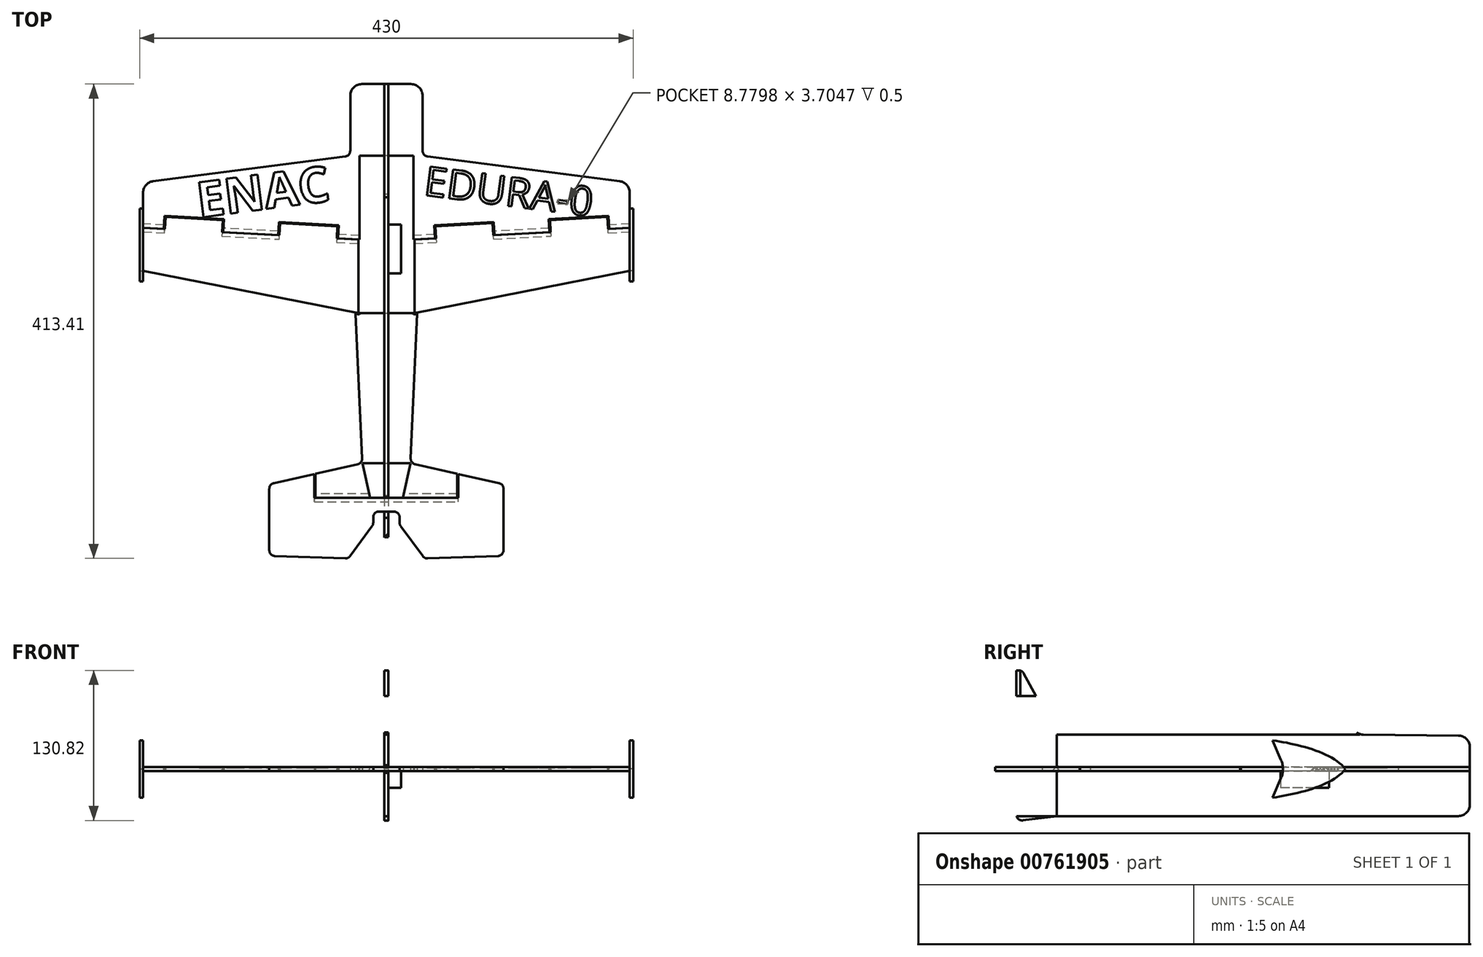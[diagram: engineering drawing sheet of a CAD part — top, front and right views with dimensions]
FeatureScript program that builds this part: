
annotation { "Feature Type Name" : "Feature", "Feature Type Description" : "" }
export const myFeature = defineFeature(function(context is Context, id is Id, definition is map)
    precondition{}
    {
        {
            assignVariable(context, id + "F0", {"name" : "strength", "anyValue" : 3.5 * mm});
        }
        {
            var Q0;
            Q0=qCreatedBy(makeId("Top.planeOp"),FACE);
            var sketch = newSketch(context, id + "F1", { "sketchPlane" : qUnion([Q0])});
            skLineSegment(sketch, "E0.bottom", {"start": v(31.5, 68.5) * mm, "end": v(-31.5, 68.5) * mm});
            skPoint(sketch, "E0.middle", {"position": v(0, 0) * mm});
            skLineSegment(sketch, "E1", {"start": v(-35.86, 67.94) * mm, "end": v(-203.28, 46.3) * mm});
            skLineSegment(sketch, "E2", {"start": v(-212, 36.4) * mm, "end": v(-212, -31.82) * mm});
            skLineSegment(sketch, "E3.MirrorCS", {"start": v(35.86, 67.94) * mm, "end": v(203.28, 46.3) * mm});
            skLineSegment(sketch, "E4.MirrorCS", {"start": v(212, 36.4) * mm, "end": v(212, -31.82) * mm});
            skLineSegment(sketch, "E5.bottom", {"start": v(-31.5, 68.5) * mm, "end": v(31.5, 68.5) * mm});
            skLineSegment(sketch, "E5.top", {"start": v(-21.5, 131) * mm, "end": v(21.5, 131) * mm});
            skLineSegment(sketch, "E5.left", {"start": v(-31.5, 72.9) * mm, "end": v(-31.5, 121) * mm});
            skLineSegment(sketch, "E5.right", {"start": v(31.5, 72.9) * mm, "end": v(31.5, 121) * mm});
            skLineSegment(sketch, "E6.top", {"start": v(-21, -199.5) * mm, "end": v(21, -199.5) * mm});
            skLineSegment(sketch, "E7", {"start": v(26.75, -69.08) * mm, "end": v(21.18, -195.31) * mm});
            skLineSegment(sketch, "E8", {"start": v(-26.75, -69.08) * mm, "end": v(-21.18, -195.31) * mm});
            skPoint(sketch, "E9.visualSharp", {"position": v(31.5, 131) * mm});
            skArc(sketch, "E9.filletArc", {"start": v(31.5, 121) * mm, "mid": v(28.57, 128.07) * mm, "end": v(21.5, 131) * mm});
            skPoint(sketch, "E10.visualSharp", {"position": v(-31.5, 131) * mm});
            skArc(sketch, "E10.filletArc", {"start": v(-21.5, 131) * mm, "mid": v(-28.57, 128.07) * mm, "end": v(-31.5, 121) * mm});
            skPoint(sketch, "E11.visualSharp", {"position": v(-212, 45.18) * mm});
            skArc(sketch, "E11.filletArc", {"start": v(-203.28, 46.3) * mm, "mid": v(-209.51, 43) * mm, "end": v(-212, 36.4) * mm});
            skPoint(sketch, "E12.visualSharp", {"position": v(212, 45.18) * mm});
            skArc(sketch, "E12.filletArc", {"start": v(212, 36.4) * mm, "mid": v(209.51, 43) * mm, "end": v(203.28, 46.3) * mm});
            skLineSegment(sketch, "E13.bottom", {"start": v(21, -199.5) * mm, "end": v(-21, -199.5) * mm});
            skLineSegment(sketch, "E14", {"start": v(-102, -221.62) * mm, "end": v(-102, -275.28) * mm});
            skLineSegment(sketch, "E15", {"start": v(-97.17, -280.28) * mm, "end": v(-35.88, -282.4) * mm});
            skLineSegment(sketch, "E16.MirrorCS", {"start": v(102, -221.62) * mm, "end": v(102, -275.28) * mm});
            skLineSegment(sketch, "E17.MirrorCS", {"start": v(97.17, -280.28) * mm, "end": v(35.88, -282.4) * mm});
            skPoint(sketch, "E18", {"position": v(0, 68.5) * mm});
            skPoint(sketch, "E19", {"position": v(0, -68.5) * mm});
            skPoint(sketch, "E20.visualSharp", {"position": v(102, -217.61) * mm});
            skArc(sketch, "E20.filletArc", {"start": v(102, -221.62) * mm, "mid": v(100.9, -218.5) * mm, "end": v(98.1, -216.74) * mm});
            skPoint(sketch, "E21.visualSharp", {"position": v(-102, -217.61) * mm});
            skArc(sketch, "E21.filletArc", {"start": v(-98.1, -216.74) * mm, "mid": v(-100.9, -218.5) * mm, "end": v(-102, -221.62) * mm});
            skLineSegment(sketch, "E22", {"start": v(6.5, -241.5) * mm, "end": v(-6.5, -241.5) * mm});
            skLineSegment(sketch, "E23", {"start": v(-21, -199.5) * mm, "end": v(-11.5, -241.5) * mm});
            skLineSegment(sketch, "E24", {"start": v(-11.5, -246.5) * mm, "end": v(-11.5, -251.36) * mm});
            skLineSegment(sketch, "E25", {"start": v(-12.48, -254.32) * mm, "end": v(-31.69, -280.38) * mm});
            skLineSegment(sketch, "E26.MirrorCS", {"start": v(21, -199.5) * mm, "end": v(11.5, -241.5) * mm});
            skLineSegment(sketch, "E27.MirrorCS", {"start": v(11.5, -246.5) * mm, "end": v(11.5, -251.36) * mm});
            skLineSegment(sketch, "E28.MirrorCS", {"start": v(12.48, -254.32) * mm, "end": v(31.69, -280.38) * mm});
            skPoint(sketch, "E29.visualSharp", {"position": v(-102, -280.11) * mm});
            skArc(sketch, "E29.filletArc", {"start": v(-102, -275.28) * mm, "mid": v(-100.6, -278.76) * mm, "end": v(-97.17, -280.28) * mm});
            skPoint(sketch, "E30.visualSharp", {"position": v(102, -280.11) * mm});
            skArc(sketch, "E30.filletArc", {"start": v(97.17, -280.28) * mm, "mid": v(100.6, -278.76) * mm, "end": v(102, -275.28) * mm});
            skPoint(sketch, "E31.visualSharp", {"position": v(33.25, -282.5) * mm});
            skArc(sketch, "E31.filletArc", {"start": v(31.69, -280.38) * mm, "mid": v(33.53, -281.91) * mm, "end": v(35.88, -282.4) * mm});
            skPoint(sketch, "E32.visualSharp", {"position": v(-33.25, -282.5) * mm});
            skArc(sketch, "E32.filletArc", {"start": v(-35.88, -282.4) * mm, "mid": v(-33.53, -281.91) * mm, "end": v(-31.69, -280.38) * mm});
            skPoint(sketch, "E33.visualSharp", {"position": v(11.5, -241.5) * mm});
            skArc(sketch, "E33.filletArc", {"start": v(11.5, -246.5) * mm, "mid": v(10.04, -242.96) * mm, "end": v(6.5, -241.5) * mm});
            skPoint(sketch, "E34.visualSharp", {"position": v(-11.5, -241.5) * mm});
            skArc(sketch, "E34.filletArc", {"start": v(-6.5, -241.5) * mm, "mid": v(-10.04, -242.96) * mm, "end": v(-11.5, -246.5) * mm});
            skPoint(sketch, "E35.visualSharp", {"position": v(-11.5, -253) * mm});
            skArc(sketch, "E35.filletArc", {"start": v(-12.48, -254.32) * mm, "mid": v(-11.75, -252.92) * mm, "end": v(-11.5, -251.36) * mm});
            skPoint(sketch, "E36.visualSharp", {"position": v(11.5, -253) * mm});
            skArc(sketch, "E36.filletArc", {"start": v(11.5, -251.36) * mm, "mid": v(11.75, -252.92) * mm, "end": v(12.48, -254.32) * mm});
            skPoint(sketch, "E37.visualSharp", {"position": v(31.5, 68.5) * mm});
            skArc(sketch, "E37.filletArc", {"start": v(31.5, 72.9) * mm, "mid": v(32.74, 69.6) * mm, "end": v(35.86, 67.94) * mm});
            skPoint(sketch, "E38.visualSharp", {"position": v(-31.5, 68.5) * mm});
            skArc(sketch, "E38.filletArc", {"start": v(-35.86, 67.94) * mm, "mid": v(-32.74, 69.6) * mm, "end": v(-31.5, 72.9) * mm});
            skLineSegment(sketch, "E39", {"start": v(-61.75, -208.61) * mm, "end": v(-61.75, -229.5) * mm});
            skLineSegment(sketch, "E40.MirrorCS", {"start": v(61.75, -208.61) * mm, "end": v(61.75, -229.5) * mm});
            skLineSegment(sketch, "E41", {"start": v(-61.75, -229.5) * mm, "end": v(61.75, -229.5) * mm});
            skLineSegment(sketch, "E42", {"start": v(-61.75, -229.5) * mm, "end": v(-62.75, -229.5) * mm});
            skLineSegment(sketch, "E43", {"start": v(-62.75, -229.5) * mm, "end": v(-62.75, -208.83) * mm});
            skLineSegment(sketch, "E44", {"start": v(-25.09, -200.41) * mm, "end": v(-61.75, -208.61) * mm});
            skLineSegment(sketch, "E45", {"start": v(-98.1, -216.74) * mm, "end": v(-62.75, -208.83) * mm});
            skLineSegment(sketch, "E46.MirrorCS", {"start": v(25.09, -200.41) * mm, "end": v(61.75, -208.61) * mm});
            skLineSegment(sketch, "E47.MirrorCS", {"start": v(98.1, -216.74) * mm, "end": v(62.75, -208.83) * mm});
            skLineSegment(sketch, "E48.MirrorCS", {"start": v(62.75, -229.5) * mm, "end": v(62.75, -208.83) * mm});
            skLineSegment(sketch, "E49.MirrorCS", {"start": v(61.75, -229.5) * mm, "end": v(62.75, -229.5) * mm});
            skLineSegment(sketch, "E50.bottom", {"start": v(-23.5, 68.5) * mm, "end": v(23.5, 68.5) * mm});
            skLineSegment(sketch, "E50.top", {"start": v(-23.5, -68.5) * mm, "end": v(23.5, -68.5) * mm});
            skLineSegment(sketch, "E50.left", {"start": v(-23.5, 68.5) * mm, "end": v(-23.5, -68.5) * mm});
            skLineSegment(sketch, "E50.right", {"start": v(23.5, 68.5) * mm, "end": v(23.5, -68.5) * mm});
            skLineSegment(sketch, "E51", {"start": v(-24.5, -68.5) * mm, "end": v(-24.5, -4.5) * mm});
            skLineSegment(sketch, "E52", {"start": v(-212, -31.82) * mm, "end": v(-24.5, -68.5) * mm});
            skLineSegment(sketch, "E53", {"start": v(-23.5, -68.5) * mm, "end": v(-23.45, -69.73) * mm});
            skLineSegment(sketch, "E54", {"start": v(-23.45, -69.73) * mm, "end": v(-26.75, -69.08) * mm});
            skLineSegment(sketch, "E55", {"start": v(-193.03, 4.7) * mm, "end": v(-192.46, 15.19) * mm});
            skLineSegment(sketch, "E56", {"start": v(-192.46, 15.19) * mm, "end": v(-142.53, 12.46) * mm});
            skLineSegment(sketch, "E57", {"start": v(-142.53, 12.46) * mm, "end": v(-143.1, 1.98) * mm});
            skLineSegment(sketch, "E58", {"start": v(-212, 5.74) * mm, "end": v(-193.03, 4.7) * mm});
            skLineSegment(sketch, "E59", {"start": v(-143.1, 1.98) * mm, "end": v(-93.18, -0.75) * mm});
            skLineSegment(sketch, "E60", {"start": v(-93.18, -0.75) * mm, "end": v(-92.6, 9.73) * mm});
            skLineSegment(sketch, "E61", {"start": v(-92.6, 9.73) * mm, "end": v(-42.68, 7) * mm});
            skLineSegment(sketch, "E62", {"start": v(-42.68, 7) * mm, "end": v(-43.25, -3.48) * mm});
            skLineSegment(sketch, "E63", {"start": v(-43.25, -3.48) * mm, "end": v(-24.5, -4.5) * mm});
            skLineSegment(sketch, "E64.0", {"start": v(-141.48, 13.4) * mm, "end": v(-142.1, 1.92) * mm});
            skLineSegment(sketch, "E64.1", {"start": v(-193.4, 16.24) * mm, "end": v(-141.48, 13.4) * mm});
            skLineSegment(sketch, "E64.2", {"start": v(-194.03, 4.76) * mm, "end": v(-193.4, 16.24) * mm});
            skLineSegment(sketch, "E65.0", {"start": v(-41.63, 7.95) * mm, "end": v(-42.25, -3.53) * mm});
            skLineSegment(sketch, "E65.1", {"start": v(-93.55, 10.79) * mm, "end": v(-41.63, 7.95) * mm});
            skLineSegment(sketch, "E65.2", {"start": v(-94.18, -0.7) * mm, "end": v(-93.55, 10.79) * mm});
            skLineSegment(sketch, "E66", {"start": v(-24.5, -4.5) * mm, "end": v(-23.5, -4.55) * mm});
            skLineSegment(sketch, "E67.MirrorCS", {"start": v(212, -31.82) * mm, "end": v(24.5, -68.5) * mm});
            skLineSegment(sketch, "E68.MirrorCS", {"start": v(212, 5.74) * mm, "end": v(193.03, 4.7) * mm});
            skLineSegment(sketch, "E69.MirrorCS", {"start": v(193.03, 4.7) * mm, "end": v(192.46, 15.19) * mm});
            skLineSegment(sketch, "E70.MirrorCS", {"start": v(192.46, 15.19) * mm, "end": v(142.53, 12.46) * mm});
            skLineSegment(sketch, "E71.MirrorCS", {"start": v(142.53, 12.46) * mm, "end": v(143.1, 1.98) * mm});
            skLineSegment(sketch, "E72.MirrorCS", {"start": v(143.1, 1.98) * mm, "end": v(93.18, -0.75) * mm});
            skLineSegment(sketch, "E73.MirrorCS", {"start": v(93.18, -0.75) * mm, "end": v(92.6, 9.73) * mm});
            skLineSegment(sketch, "E74.MirrorCS", {"start": v(92.6, 9.73) * mm, "end": v(42.68, 7) * mm});
            skLineSegment(sketch, "E75.MirrorCS", {"start": v(42.68, 7) * mm, "end": v(43.25, -3.48) * mm});
            skLineSegment(sketch, "E76.MirrorCS", {"start": v(43.25, -3.48) * mm, "end": v(24.5, -4.5) * mm});
            skLineSegment(sketch, "E77.MirrorCS", {"start": v(24.5, -68.5) * mm, "end": v(24.5, -4.5) * mm});
            skLineSegment(sketch, "E78.MirrorCS", {"start": v(23.5, -68.5) * mm, "end": v(23.45, -69.73) * mm});
            skLineSegment(sketch, "E79.MirrorCS", {"start": v(23.45, -69.73) * mm, "end": v(26.75, -69.08) * mm});
            skLineSegment(sketch, "E80.MirrorCS", {"start": v(41.63, 7.95) * mm, "end": v(42.25, -3.53) * mm});
            skLineSegment(sketch, "E81.MirrorCS", {"start": v(93.55, 10.79) * mm, "end": v(41.63, 7.95) * mm});
            skLineSegment(sketch, "E82.MirrorCS", {"start": v(94.18, -0.7) * mm, "end": v(93.55, 10.79) * mm});
            skLineSegment(sketch, "E83.MirrorCS", {"start": v(141.48, 13.4) * mm, "end": v(142.1, 1.92) * mm});
            skLineSegment(sketch, "E84.MirrorCS", {"start": v(193.4, 16.24) * mm, "end": v(141.48, 13.4) * mm});
            skLineSegment(sketch, "E85.MirrorCS", {"start": v(194.03, 4.76) * mm, "end": v(193.4, 16.24) * mm});
            skLineSegment(sketch, "E86.MirrorCS", {"start": v(24.5, -4.5) * mm, "end": v(23.5, -4.55) * mm});
            skPoint(sketch, "E87.visualSharp", {"position": v(21, -199.5) * mm});
            skArc(sketch, "E87.filletArc", {"start": v(21.18, -195.31) * mm, "mid": v(22.2, -198.57) * mm, "end": v(25.09, -200.41) * mm});
            skPoint(sketch, "E88.visualSharp", {"position": v(-21, -199.5) * mm});
            skArc(sketch, "E88.filletArc", {"start": v(-25.09, -200.41) * mm, "mid": v(-22.2, -198.57) * mm, "end": v(-21.18, -195.31) * mm});
            skSolve(sketch);
        }
        {
            var Q0;
            Q0=makeQuery(id+"F1.imprint","IMPRINT",FACE,{"disambiguationData":[TD([[makeQuery(id+"F1.imprint","IMPRINT",EDGE,{"derivedFrom":sQuery(id+"F1.wireOp",EDGE,"E1")}),1.0]])]});
            var Q1;
            Q1=makeQuery(id+"F1.imprint","IMPRINT",FACE,{"disambiguationData":[TD([[makeQuery(id+"F1.imprint","IMPRINT",EDGE,{"derivedFrom":sQuery(id+"F1.wireOp",EDGE,"E5.bottom")}),-1.0]])]});
            var Q2;
            Q2=makeQuery(id+"F1.imprint","IMPRINT",FACE,{"disambiguationData":[TD([[makeQuery(id+"F1.imprint","IMPRINT",EDGE,{"derivedFrom":sQuery(id+"F1.wireOp",EDGE,"E6.bottom")}),-1.0]])]});
            var Q3;
            {var subQ4=sQuery(id+"F1.wireOp",EDGE,"E39");Q3=makeQuery(id+"F1.imprint","IMPRINT",FACE,{"disambiguationData":[TD([[makeQuery(id+"F1.imprint","IMPRINT",EDGE,{"derivedFrom":subQ4}),1.0]])]});}
            var Q4;
            {var subQ4=sQuery(id+"F1.wireOp",EDGE,"E40.MirrorCS");Q4=makeQuery(id+"F1.imprint","IMPRINT",FACE,{"disambiguationData":[TD([[makeQuery(id+"F1.imprint","IMPRINT",EDGE,{"derivedFrom":subQ4}),-1.0]])]});}
            var Q5;
            {var subQ0=sQuery(id+"F1.wireOp",EDGE,"E13.bottom");Q5=makeQuery(id+"F1.imprint","IMPRINT",FACE,{"disambiguationData":[TD([[makeQuery(id+"F1.imprint","IMPRINT",EDGE,{"derivedFrom":subQ0}),1.0]])]});}
            var Q6;
            {var subQ3=sQuery(id+"F1.wireOp",EDGE,"E50.bottom");Q6=makeQuery(id+"F1.imprint","IMPRINT",FACE,{"disambiguationData":[TD([[makeQuery(id+"F1.imprint","IMPRINT",EDGE,{"derivedFrom":subQ3}),-1.0]])]});}
            extrude(context, id + "F2", {"entities" : qUnion([Q0, Q1, Q2, Q3, Q4, Q5, Q6]), "endBound" : BoundingType.SYMMETRIC, "depth" : getVariable(context, 'strength'), "offsetDistance" : 25 * mm});
        }
        {
            var Q0;
            Q0=makeQuery(id+"F1.imprint","IMPRINT",FACE,{"disambiguationData":[TD([[makeQuery(id+"F1.imprint","IMPRINT",EDGE,{"derivedFrom":sQuery(id+"F1.wireOp",EDGE,"E14")}),1.0]])]});
            extrude(context, id + "F3", {"entities" : qUnion([Q0]), "endBound" : BoundingType.SYMMETRIC, "depth" : getVariable(context, 'strength'), "offsetDistance" : 25 * mm});
        }
        {
            var Q0;
            {var subQ10=sQuery(id+"F1.wireOp",EDGE,"E51");Q0=makeQuery(id+"F1.imprint","IMPRINT",FACE,{"disambiguationData":[TD([[makeQuery(id+"F1.imprint","IMPRINT",EDGE,{"derivedFrom":subQ10}),1.0]])]});}
            var Q1;
            {var subQ6=sQuery(id+"F1.wireOp",EDGE,"E67.MirrorCS");Q1=makeQuery(id+"F1.imprint","IMPRINT",FACE,{"disambiguationData":[TD([[makeQuery(id+"F1.imprint","IMPRINT",EDGE,{"derivedFrom":subQ6}),-1.0]])]});}
            extrude(context, id + "F4", {"entities" : qUnion([Q0, Q1]), "endBound" : BoundingType.SYMMETRIC, "depth" : getVariable(context, 'strength'), "offsetDistance" : 25 * mm});
        }
        {
            var Q0;
            Q0=makeQuery(id+"F2.opExtrude","SWEPT_FACE",FACE,{"disambiguationData":[OSD([sQuery(id+"F1.wireOp",EDGE,"E2")])]});
            var sketch = newSketch(context, id + "F5", { "sketchPlane" : qUnion([Q0])});
            skFitSpline(sketch, "E89", {"points": [v(-22.68, 0) * mm, v(40.82, -25) * mm], "startDerivative": vector(34.06, -43.9) * mm, "endDerivative": vector(67.73, -10.43) * mm});
            skFitSpline(sketch, "E90.MirrorCS", {"points": [v(-22.68, 0) * mm, v(40.82, 25) * mm], "startDerivative": vector(34.06, 43.9) * mm, "endDerivative": vector(67.73, 10.43) * mm});
            skLineSegment(sketch, "E91", {"start": v(33.45, 7.92) * mm, "end": v(40.82, 25) * mm});
            skLineSegment(sketch, "E92.MirrorCS", {"start": v(33.45, -7.92) * mm, "end": v(40.82, -25) * mm});
            skPoint(sketch, "E93.visualSharp", {"position": v(30.04, 0) * mm});
            skArc(sketch, "E93.filletArc", {"start": v(33.45, 7.92) * mm, "mid": v(31.82, 0) * mm, "end": v(33.45, -7.92) * mm});
            skPoint(sketch, "E94", {"position": v(31.82, 0) * mm});
            skSolve(sketch);
        }
        {
            var Q0;
            {var subQ5=sQuery(id+"F5.wireOp",EDGE,"E90.MirrorCS");var subQ6=sQuery(id+"F5.wireOp",EDGE,"E89");var subQ7=makeQuery(id+"F5.imprint","INTERSECT",VERTEX,{"derivedFrom":[subQ6,subQ5]});Q0=makeQuery(id+"F5.imprint","IMPRINT",FACE,{"disambiguationData":[TD([[makeQuery(id+"F5.imprint","IMPRINT",EDGE,{"disambiguationData":[TD([[subQ7,-1.0]])],"derivedFrom":subQ6}),1.0]])]});}
            var Q1;
            {var subQ6=sQuery(id+"F5.wireOp",EDGE,"0b6l1ef1-qT08-gGJA-z1ug-tlMFagzUV6Nq");Q1=makeQuery(id+"F5.imprint","IMPRINT",FACE,{"disambiguationData":[TD([[makeQuery(id+"F5.imprint","IMPRINT",EDGE,{"derivedFrom":subQ6}),-1.0]])]});}
            var Q2;
            {var subQ6=sQuery(id+"F5.wireOp",EDGE,"CPXi0MRo-90Zd-YapA-SOgp-mV6B9kNiCjMr");Q2=makeQuery(id+"F5.imprint","IMPRINT",FACE,{"disambiguationData":[TD([[makeQuery(id+"F5.imprint","IMPRINT",EDGE,{"derivedFrom":subQ6}),-1.0]])]});}
            var Q3;
            {var subQ1=sQuery(id+"F5.wireOp",EDGE,"E91");Q3=makeQuery(id+"F5.imprint","IMPRINT",FACE,{"disambiguationData":[TD([[makeQuery(id+"F5.imprint","IMPRINT",EDGE,{"derivedFrom":subQ1}),1.0]])]});}
            extrude(context, id + "F6", {"entities" : qUnion([Q0, Q1, Q2, Q3]), "depth" : 3 * mm, "offsetDistance" : 25 * mm});
        }
        {
            var Q0;
            Q0=makeQuery(id+"F6.opExtrude","SWEPT_BODY",BODY,{"disambiguationData":[OSD([sQuery(id+"F5.wireOp",EDGE,"E89"),sQuery(id+"F5.wireOp",EDGE,"E90.MirrorCS"),sQuery(id+"F5.wireOp",EDGE,"1s8DE9hj-UFXd-2Cyi-hbdZ-TRl4sMV5K9nb"),sQuery(id+"F5.wireOp",EDGE,"i6L2f3uI-2JMr-tqse-sLL8-sHchnDCTj292"),sQuery(id+"F5.wireOp",EDGE,"9655445b-8ee7-467b-abd0-545b39a3ffc4.filletArc")])]});
            var Q1;
            Q1=qCreatedBy(makeId("Right.planeOp"),FACE);
            mirror(context, id + "F7", {"entities" : qUnion([Q0]), "mirrorPlane" : qUnion([Q1])});
        }
        {
            var Q0;
            Q0=qCreatedBy(makeId("Right.planeOp"),FACE);
            var sketch = newSketch(context, id + "F8", { "sketchPlane" : qUnion([Q0])});
            skLineSegment(sketch, "E95.bottom", {"start": v(121, -41) * mm, "end": v(-229, -41) * mm});
            skLineSegment(sketch, "E95.left", {"start": v(131, -31) * mm, "end": v(131, 19.1) * mm});
            skLineSegment(sketch, "E95.right", {"start": v(-229, -41) * mm, "end": v(-229, 30) * mm});
            skPoint(sketch, "E96", {"position": v(35, 30) * mm});
            skPoint(sketch, "E97", {"position": v(-19, 60) * mm});
            skLineSegment(sketch, "E98", {"start": v(35, 30) * mm, "end": v(35, -41) * mm});
            skLineSegment(sketch, "E99", {"start": v(121.1, 29.1) * mm, "end": v(38.21, 29.97) * mm});
            skLineSegment(sketch, "E100", {"start": v(-229, 30) * mm, "end": v(35, 30) * mm});
            skFitSpline(sketch, "E101", {"points": [v(35, 30) * mm, v(-19, 60) * mm, v(-229, 30) * mm], "startDerivative": vector(-145.14, 104.61) * mm, "endDerivative": vector(-364.1, -88.1) * mm});
            skPoint(sketch, "E102.visualSharp", {"position": v(131, -41) * mm});
            skArc(sketch, "E102.filletArc", {"start": v(121, -41) * mm, "mid": v(128.07, -38.07) * mm, "end": v(131, -31) * mm});
            skPoint(sketch, "E103.visualSharp", {"position": v(131, 29) * mm});
            skArc(sketch, "E103.filletArc", {"start": v(131, 19.1) * mm, "mid": v(128.1, 26.14) * mm, "end": v(121.1, 29.1) * mm});
            skArc(sketch, "E104.filletArc", {"start": v(32.35, 31.94) * mm, "mid": v(35.13, 30.49) * mm, "end": v(38.21, 29.97) * mm});
            skLineSegment(sketch, "E105", {"start": v(-229, -41) * mm, "end": v(-264, -41) * mm});
            skLineSegment(sketch, "E106", {"start": v(-264, -41) * mm, "end": v(-264, 86) * mm});
            skLineSegment(sketch, "E107", {"start": v(-264, -39.82) * mm, "end": v(-264, -41) * mm});
            skLineSegment(sketch, "E108", {"start": v(-258.36, -44.78) * mm, "end": v(-229, -41) * mm});
            skLineSegment(sketch, "E109", {"start": v(-264, 86) * mm, "end": v(-262, 86) * mm});
            skLineSegment(sketch, "E110", {"start": v(-264, 86) * mm, "end": v(-309.75, 86) * mm});
            skLineSegment(sketch, "E111", {"start": v(-314.68, 81.8) * mm, "end": v(-332.22, -26.38) * mm});
            skLineSegment(sketch, "E112", {"start": v(-322.86, -37.96) * mm, "end": v(-264, -41) * mm});
            skPoint(sketch, "E113", {"position": v(-227.5, 0) * mm});
            skArc(sketch, "E114", {"start": v(-242.5, 0) * mm, "mid": v(-240.05, 8.22) * mm, "end": v(-233.5, 13.75) * mm});
            skLineSegment(sketch, "E115", {"start": v(-227.5, 0) * mm, "end": v(-233.5, 13.75) * mm});
            skLineSegment(sketch, "E116.MirrorCS", {"start": v(-227.5, 0) * mm, "end": v(-233.5, -13.75) * mm});
            skArc(sketch, "E117.MirrorCS", {"start": v(-242.5, 0) * mm, "mid": v(-240.05, -8.22) * mm, "end": v(-233.5, -13.75) * mm});
            skPoint(sketch, "E118.visualSharp", {"position": v(-259, 86) * mm});
            skArc(sketch, "E118.filletArc", {"start": v(-257.59, 83.36) * mm, "mid": v(-259.43, 85.29) * mm, "end": v(-262, 86) * mm});
            skArc(sketch, "E119.filletArc", {"start": v(-232.65, 36.81) * mm, "mid": v(-227.92, 32.4) * mm, "end": v(-221.5, 31.81) * mm});
            skPoint(sketch, "E120.visualSharp", {"position": v(-314, 86) * mm});
            skArc(sketch, "E120.filletArc", {"start": v(-309.75, 86) * mm, "mid": v(-312.99, 84.8) * mm, "end": v(-314.68, 81.8) * mm});
            skPoint(sketch, "E121.visualSharp", {"position": v(-334, -37.39) * mm});
            skArc(sketch, "E121.filletArc", {"start": v(-332.22, -26.38) * mm, "mid": v(-330.12, -34.26) * mm, "end": v(-322.86, -37.96) * mm});
            skPoint(sketch, "E122.visualSharp", {"position": v(-264, -45.5) * mm});
            skArc(sketch, "E122.filletArc", {"start": v(-264, -39.82) * mm, "mid": v(-262.3, -43.57) * mm, "end": v(-258.36, -44.78) * mm});
            skLineSegment(sketch, "E123", {"start": v(-264, 62.75) * mm, "end": v(-246.54, 62.75) * mm});
            skLineSegment(sketch, "E124", {"start": v(-264, 63.75) * mm, "end": v(-247.08, 63.75) * mm});
            skLineSegment(sketch, "E125", {"start": v(-232.65, 36.81) * mm, "end": v(-246.54, 62.75) * mm});
            skLineSegment(sketch, "E126", {"start": v(-247.08, 63.75) * mm, "end": v(-257.59, 83.36) * mm});
            skSolve(sketch);
        }
        {
            var Q0;
            Q0=makeQuery(id+"F8.imprint","IMPRINT",FACE,{"disambiguationData":[TD([[makeQuery(id+"F8.imprint","IMPRINT",EDGE,{"derivedFrom":sQuery(id+"F8.wireOp",EDGE,"E95.left")}),1.0]])]});
            var Q1;
            {var subQ0=sQuery(id+"F8.wireOp",EDGE,"E98");Q1=makeQuery(id+"F8.imprint","IMPRINT",FACE,{"disambiguationData":[TD([[makeQuery(id+"F8.imprint","IMPRINT",EDGE,{"derivedFrom":subQ0}),-1.0]])]});}
            var Q2;
            {var subQ0=sQuery(id+"F8.wireOp",EDGE,"E108");Q2=makeQuery(id+"F8.imprint","IMPRINT",FACE,{"disambiguationData":[TD([[makeQuery(id+"F8.imprint","IMPRINT",EDGE,{"derivedFrom":subQ0}),1.0]])]});}
            extrude(context, id + "F9", {"entities" : qUnion([Q0, Q1, Q2]), "endBound" : BoundingType.SYMMETRIC, "depth" : getVariable(context, 'strength'), "offsetDistance" : 25 * mm});
        }
        {
            var Q0;
            {var subQ0=sQuery(id+"F8.wireOp",EDGE,"E107");Q0=makeQuery(id+"F8.imprint","IMPRINT",FACE,{"disambiguationData":[TD([[makeQuery(id+"F8.imprint","IMPRINT",EDGE,{"derivedFrom":subQ0}),-1.0]])]});}
            var Q1;
            {var subQ0=sQuery(id+"F8.wireOp",EDGE,"E109");Q1=makeQuery(id+"F8.imprint","IMPRINT",FACE,{"disambiguationData":[TD([[makeQuery(id+"F8.imprint","IMPRINT",EDGE,{"derivedFrom":subQ0}),-1.0]])]});}
            extrude(context, id + "F10", {"entities" : qUnion([Q0, Q1]), "endBound" : BoundingType.SYMMETRIC, "depth" : getVariable(context, 'strength'), "offsetDistance" : 25 * mm});
        }
        {
            var Q0;
            Q0=makeQuery(id+"F2.opExtrude","CAP_EDGE",EDGE,{"disambiguationData":[OSD([sQuery(id+"F1.wireOp",EDGE,"E41")])],"isStart":true});
            var Q1;
            Q1=makeQuery(id+"F2.opExtrude","CAP_EDGE",EDGE,{"disambiguationData":[OSD([sQuery(id+"F1.wireOp",EDGE,"E68.MirrorCS")])],"isStart":true});
            var Q2;
            Q2=makeQuery(id+"F2.opExtrude","CAP_EDGE",EDGE,{"disambiguationData":[OSD([sQuery(id+"F1.wireOp",EDGE,"E72.MirrorCS")])],"isStart":true});
            var Q3;
            Q3=makeQuery(id+"F9.opExtrude","CAP_EDGE",EDGE,{"disambiguationData":[OSD([sQuery(id+"F8.wireOp",EDGE,"E106")])],"isStart":false});
            var Q4;
            Q4=makeQuery(id+"F2.opExtrude","CAP_EDGE",EDGE,{"disambiguationData":[OSD([sQuery(id+"F1.wireOp",EDGE,"E63"),sQuery(id+"F1.wireOp",EDGE,"E66")])],"isStart":true});
            var Q5;
            Q5=makeQuery(id+"F2.opExtrude","CAP_EDGE",EDGE,{"disambiguationData":[OSD([sQuery(id+"F1.wireOp",EDGE,"E59")])],"isStart":true});
            var Q6;
            Q6=makeQuery(id+"F2.opExtrude","CAP_EDGE",EDGE,{"disambiguationData":[OSD([sQuery(id+"F1.wireOp",EDGE,"E58")])],"isStart":true});
            var Q7;
            Q7=makeQuery(id+"F2.opExtrude","CAP_EDGE",EDGE,{"disambiguationData":[OSD([sQuery(id+"F1.wireOp",EDGE,"E76.MirrorCS"),sQuery(id+"F1.wireOp",EDGE,"E86.MirrorCS")])],"isStart":true});
            chamfer(context, id + "F11", {"entities" : qUnion([Q0, Q1, Q2, Q3, Q4, Q5, Q6, Q7]), "width" : getVariable(context, 'strength'), "tangentPropagation" : true});
        }
        {
            var Q0;
            Q0=makeQuery(id+"F10.opExtrude","CAP_EDGE",EDGE,{"disambiguationData":[OSD([sQuery(id+"F8.wireOp",EDGE,"E106"),sQuery(id+"F8.wireOp",EDGE,"E107")])],"isStart":false});
            var Q1;
            Q1=makeQuery(id+"F3.opExtrude","CAP_EDGE",EDGE,{"disambiguationData":[OSD([sQuery(id+"F1.wireOp",EDGE,"E41"),sQuery(id+"F1.wireOp",EDGE,"E42"),sQuery(id+"F1.wireOp",EDGE,"E49.MirrorCS")])],"isStart":true});
            var Q2;
            Q2=makeQuery(id+"F4.opExtrude","CAP_EDGE",EDGE,{"disambiguationData":[OSD([sQuery(id+"F1.wireOp",EDGE,"E68.MirrorCS")])],"isStart":true});
            var Q3;
            Q3=makeQuery(id+"F4.opExtrude","CAP_EDGE",EDGE,{"disambiguationData":[OSD([sQuery(id+"F1.wireOp",EDGE,"E72.MirrorCS")])],"isStart":true});
            var Q4;
            Q4=makeQuery(id+"F4.opExtrude","CAP_EDGE",EDGE,{"disambiguationData":[OSD([sQuery(id+"F1.wireOp",EDGE,"E76.MirrorCS")])],"isStart":true});
            var Q5;
            Q5=makeQuery(id+"F4.opExtrude","CAP_EDGE",EDGE,{"disambiguationData":[OSD([sQuery(id+"F1.wireOp",EDGE,"E58")])],"isStart":true});
            var Q6;
            Q6=makeQuery(id+"F4.opExtrude","CAP_EDGE",EDGE,{"disambiguationData":[OSD([sQuery(id+"F1.wireOp",EDGE,"E59")])],"isStart":true});
            var Q7;
            Q7=makeQuery(id+"F4.opExtrude","CAP_EDGE",EDGE,{"disambiguationData":[OSD([sQuery(id+"F1.wireOp",EDGE,"E63")])],"isStart":true});
            chamfer(context, id + "F12", {"entities" : qUnion([Q0, Q1, Q2, Q3, Q4, Q5, Q6, Q7]), "width" : getVariable(context, 'strength'), "tangentPropagation" : true});
        }
        {
            var Q0;
            Q0=makeQuery(id+"F10.opExtrude","CAP_FACE",FACE,{"disambiguationData":[OSD([sQuery(id+"F8.wireOp",EDGE,"E106"),sQuery(id+"F8.wireOp",EDGE,"E107"),sQuery(id+"F8.wireOp",EDGE,"E109"),sQuery(id+"F8.wireOp",EDGE,"E110"),sQuery(id+"F8.wireOp",EDGE,"E111"),sQuery(id+"F8.wireOp",EDGE,"E112"),sQuery(id+"F8.wireOp",EDGE,"E118.filletArc"),sQuery(id+"F8.wireOp",EDGE,"E120.filletArc"),sQuery(id+"F8.wireOp",EDGE,"E121.filletArc"),sQuery(id+"F8.wireOp",EDGE,"E124"),sQuery(id+"F8.wireOp",EDGE,"E126")])],"isStart":true});
            var sketch = newSketch(context, id + "F13", { "sketchPlane" : qUnion([Q0])});
            skText(sketch, "E127", { "text": "ENAC", "fontName": "OpenSans-Bold.ttf"});
            skText(sketch, "E128", { "text": "http://www.enac.fr", "fontName": "OpenSans-Regular.ttf"});
            const initialGuessF13  = {"E127": [0.3007, -0.03839, 0, 1, 0.0317], "E128": [0.31453, -0.03839, 0, 1, 0.00983]};
            skSetInitialGuess(sketch, initialGuessF13);
            skSolve(sketch);
        }
        {
            var Q0;
            Q0 = qSketchRegion(id + "F13", true);
            extrude(context, id + "F14", {"entities" : qUnion([Q0]), "operationType" : NewBodyOperationType.REMOVE, "oppositeDirection" : true, "depth" : .5 * mm, "offsetDistance" : 25 * mm});
        }
        {
            var Q0;
            Q0=makeQuery(id+"F2.opExtrude","CAP_FACE",FACE,{"disambiguationData":[OSD([sQuery(id+"F1.wireOp",EDGE,"E1"),sQuery(id+"F1.wireOp",EDGE,"E2"),sQuery(id+"F1.wireOp",EDGE,"E3.MirrorCS"),sQuery(id+"F1.wireOp",EDGE,"E4.MirrorCS"),sQuery(id+"F1.wireOp",EDGE,"E5.top"),sQuery(id+"F1.wireOp",EDGE,"E5.left"),sQuery(id+"F1.wireOp",EDGE,"E5.right"),sQuery(id+"F1.wireOp",EDGE,"E7"),sQuery(id+"F1.wireOp",EDGE,"E8"),sQuery(id+"F1.wireOp",EDGE,"E9.filletArc"),sQuery(id+"F1.wireOp",EDGE,"E10.filletArc"),sQuery(id+"F1.wireOp",EDGE,"E11.filletArc"),sQuery(id+"F1.wireOp",EDGE,"E12.filletArc"),sQuery(id+"F1.wireOp",EDGE,"E37.filletArc"),sQuery(id+"F1.wireOp",EDGE,"E38.filletArc"),sQuery(id+"F1.wireOp",EDGE,"E39"),sQuery(id+"F1.wireOp",EDGE,"E40.MirrorCS"),sQuery(id+"F1.wireOp",EDGE,"E41"),sQuery(id+"F1.wireOp",EDGE,"E44"),sQuery(id+"F1.wireOp",EDGE,"E46.MirrorCS"),sQuery(id+"F1.wireOp",EDGE,"E50.left"),sQuery(id+"F1.wireOp",EDGE,"E50.right"),sQuery(id+"F1.wireOp",EDGE,"E53"),sQuery(id+"F1.wireOp",EDGE,"E54"),sQuery(id+"F1.wireOp",EDGE,"E58"),sQuery(id+"F1.wireOp",EDGE,"E59"),sQuery(id+"F1.wireOp",EDGE,"E63"),sQuery(id+"F1.wireOp",EDGE,"E64.0"),sQuery(id+"F1.wireOp",EDGE,"E64.1"),sQuery(id+"F1.wireOp",EDGE,"E64.2"),sQuery(id+"F1.wireOp",EDGE,"E65.0"),sQuery(id+"F1.wireOp",EDGE,"E65.1"),sQuery(id+"F1.wireOp",EDGE,"E65.2"),sQuery(id+"F1.wireOp",EDGE,"E66"),sQuery(id+"F1.wireOp",EDGE,"E68.MirrorCS"),sQuery(id+"F1.wireOp",EDGE,"E72.MirrorCS"),sQuery(id+"F1.wireOp",EDGE,"E76.MirrorCS"),sQuery(id+"F1.wireOp",EDGE,"E78.MirrorCS"),sQuery(id+"F1.wireOp",EDGE,"E79.MirrorCS"),sQuery(id+"F1.wireOp",EDGE,"E80.MirrorCS"),sQuery(id+"F1.wireOp",EDGE,"E81.MirrorCS"),sQuery(id+"F1.wireOp",EDGE,"E82.MirrorCS"),sQuery(id+"F1.wireOp",EDGE,"E83.MirrorCS"),sQuery(id+"F1.wireOp",EDGE,"E84.MirrorCS"),sQuery(id+"F1.wireOp",EDGE,"E85.MirrorCS"),sQuery(id+"F1.wireOp",EDGE,"E86.MirrorCS"),sQuery(id+"F1.wireOp",EDGE,"E87.filletArc"),sQuery(id+"F1.wireOp",EDGE,"E88.filletArc")])],"isStart":false});
            var sketch = newSketch(context, id + "F15", { "sketchPlane" : qUnion([Q0])});
            skText(sketch, "E129", { "text": "ENAC", "fontName": "OpenSans-Bold.ttf"});
            skText(sketch, "E130", { "text": "EDURA-0", "fontName": "OpenSans-Regular.ttf"});
            const initialGuessF15  = {"E129": [-0.16304, 0.01458, 0.99176, 0.12812, 0.03093], "E130": [0.03175, 0.03442, 0.99176, -0.12812, 0.02557]};
            skSetInitialGuess(sketch, initialGuessF15);
            skSolve(sketch);
        }
        {
            var Q0;
            Q0 = qSketchRegion(id + "F15", true);
            extrude(context, id + "F16", {"entities" : qUnion([Q0]), "operationType" : NewBodyOperationType.REMOVE, "oppositeDirection" : true, "depth" : .5 * mm, "offsetDistance" : 25 * mm});
        }
        {
            var Q0;
            Q0=makeQuery(id+"F10.opExtrude","CAP_FACE",FACE,{"disambiguationData":[OSD([sQuery(id+"F8.wireOp",EDGE,"E106"),sQuery(id+"F8.wireOp",EDGE,"E107"),sQuery(id+"F8.wireOp",EDGE,"E109"),sQuery(id+"F8.wireOp",EDGE,"E110"),sQuery(id+"F8.wireOp",EDGE,"E111"),sQuery(id+"F8.wireOp",EDGE,"E112"),sQuery(id+"F8.wireOp",EDGE,"E118.filletArc"),sQuery(id+"F8.wireOp",EDGE,"E120.filletArc"),sQuery(id+"F8.wireOp",EDGE,"E121.filletArc"),sQuery(id+"F8.wireOp",EDGE,"E124"),sQuery(id+"F8.wireOp",EDGE,"E126")])],"isStart":false});
            var sketch = newSketch(context, id + "F17", { "sketchPlane" : qUnion([Q0])});
            skText(sketch, "E131", { "text": "ENAC", "fontName": "OpenSans-Bold.ttf"});
            skText(sketch, "E132", { "text": "http://www.enac.fr", "fontName": "OpenSans-Regular.ttf"});
            const initialGuessF17  = {"E131": [-0.28283, -0.03839, 0, 1, 0.0317], "E132": [-0.269, -0.03839, 0, 1, 0.00983]};
            skSetInitialGuess(sketch, initialGuessF17);
            skSolve(sketch);
        }
        {
            var Q0;
            Q0 = qSketchRegion(id + "F17", true);
            extrude(context, id + "F18", {"entities" : qUnion([Q0]), "operationType" : NewBodyOperationType.REMOVE, "oppositeDirection" : true, "depth" : .5 * mm, "offsetDistance" : 25 * mm});
        }
        {
            var Q0;
            Q0=makeQuery(id+"F9.opExtrude","CAP_FACE",FACE,{"disambiguationData":[OSD([sQuery(id+"F8.wireOp",EDGE,"E95.bottom"),sQuery(id+"F8.wireOp",EDGE,"E95.left"),sQuery(id+"F8.wireOp",EDGE,"E99"),sQuery(id+"F8.wireOp",EDGE,"E101"),sQuery(id+"F8.wireOp",EDGE,"E102.filletArc"),sQuery(id+"F8.wireOp",EDGE,"E103.filletArc"),sQuery(id+"F8.wireOp",EDGE,"E104.filletArc"),sQuery(id+"F8.wireOp",EDGE,"E106"),sQuery(id+"F8.wireOp",EDGE,"E108"),sQuery(id+"F8.wireOp",EDGE,"E114"),sQuery(id+"F8.wireOp",EDGE,"E115"),sQuery(id+"F8.wireOp",EDGE,"E116.MirrorCS"),sQuery(id+"F8.wireOp",EDGE,"E117.MirrorCS"),sQuery(id+"F8.wireOp",EDGE,"E119.filletArc"),sQuery(id+"F8.wireOp",EDGE,"E122.filletArc"),sQuery(id+"F8.wireOp",EDGE,"E123"),sQuery(id+"F8.wireOp",EDGE,"E125")])],"isStart":false});
            var sketch = newSketch(context, id + "F19", { "sketchPlane" : qUnion([Q0])});
            skLineSegment(sketch, "E133.bottom", {"start": v(8.5, -1.75) * mm, "end": v(-34, -1.75) * mm});
            skLineSegment(sketch, "E133.top", {"start": v(8.5, -16.5) * mm, "end": v(-34, -16.5) * mm});
            skLineSegment(sketch, "E133.left", {"start": v(8.5, -1.75) * mm, "end": v(8.5, -16.5) * mm});
            skLineSegment(sketch, "E133.right", {"start": v(-34, -1.75) * mm, "end": v(-34, -16.5) * mm});
            skLineSegment(sketch, "E134.bottom", {"start": v(-34, -1.75) * mm, "end": v(8.5, -1.75) * mm});
            skLineSegment(sketch, "E134.top", {"start": v(-34, 23.5) * mm, "end": v(8.5, 23.5) * mm});
            skLineSegment(sketch, "E134.left", {"start": v(-34, -1.75) * mm, "end": v(-34, 23.5) * mm});
            skLineSegment(sketch, "E134.right", {"start": v(8.5, -1.75) * mm, "end": v(8.5, 23.5) * mm});
            skSolve(sketch);
        }
        {
            var Q0;
            Q0=makeQuery(id+"F19.imprint","IMPRINT",FACE,{"disambiguationData":[TD([[makeQuery(id+"F19.imprint","IMPRINT",EDGE,{"derivedFrom":sQuery(id+"F19.wireOp",EDGE,"E133.top")}),-1.0]])]});
            var Q1;
            Q1=makeQuery(id+"F19.imprint","IMPRINT",FACE,{"disambiguationData":[TD([[makeQuery(id+"F19.imprint","IMPRINT",EDGE,{"derivedFrom":sQuery(id+"F19.wireOp",EDGE,"E134.bottom")}),1.0]])]});
            extrude(context, id + "F20", {"entities" : qUnion([Q0, Q1]), "operationType" : NewBodyOperationType.ADD, "depth" : 11 * mm, "offsetDistance" : 25 * mm});
        }
    });
